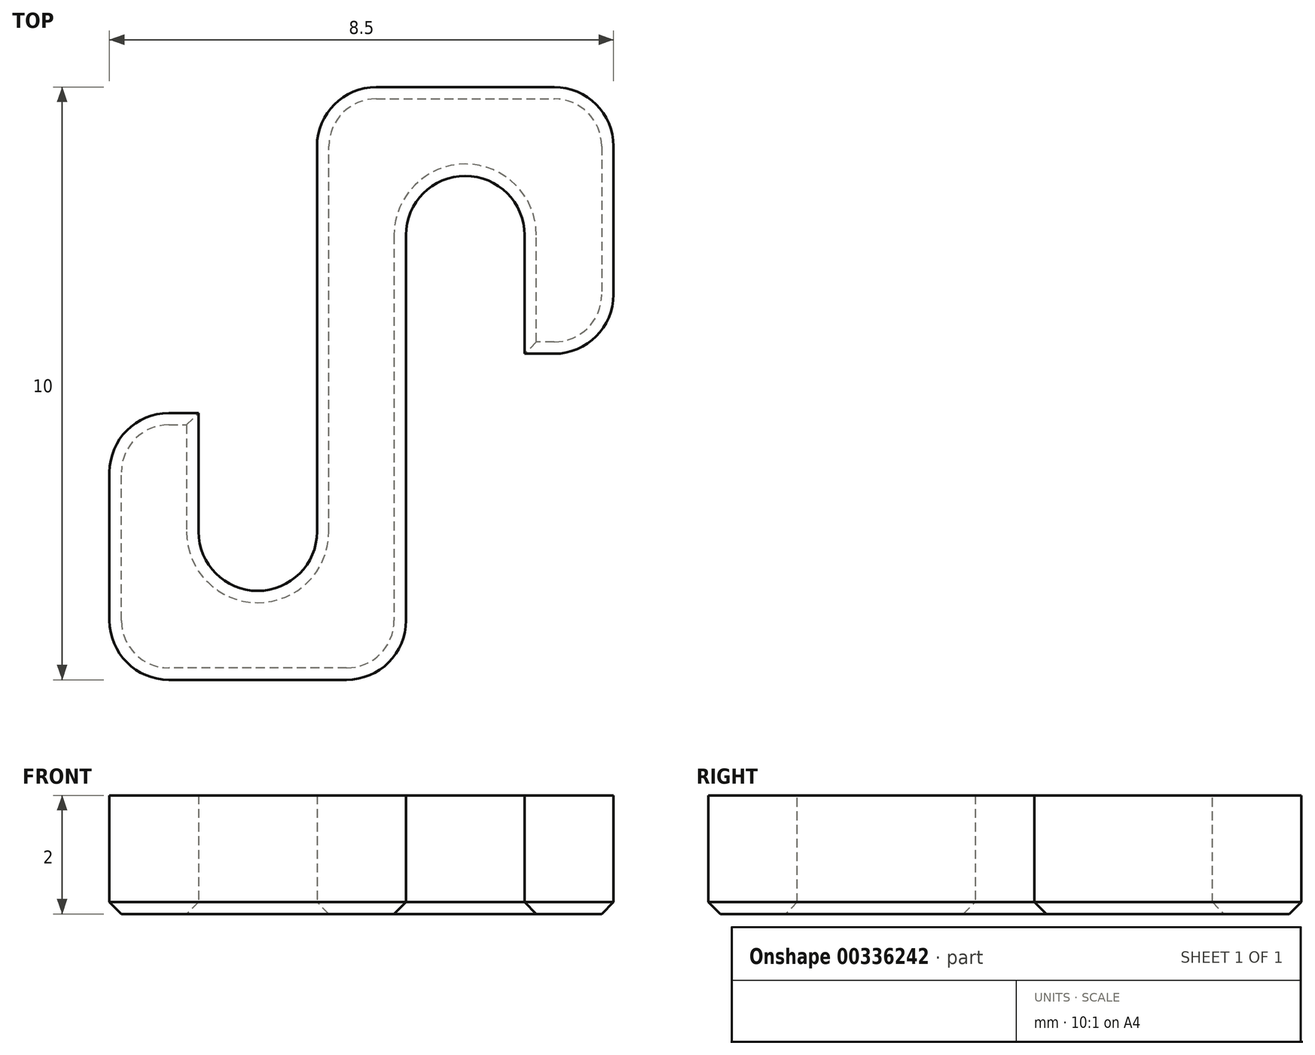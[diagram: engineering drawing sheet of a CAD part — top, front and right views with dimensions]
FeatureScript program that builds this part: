
annotation { "Feature Type Name" : "Feature", "Feature Type Description" : "" }
export const myFeature = defineFeature(function(context is Context, id is Id, definition is map)
    precondition{}
    {
        {
            var Q0;
            Q0=qCreatedBy(makeId("Top.planeOp"),FACE);
            var sketch = newSketch(context, id + "F0", { "sketchPlane" : qUnion([Q0])});
            skLineSegment(sketch, "E0", {"start": v(-0.75, 0) * mm, "end": v(-0.75, 5) * mm});
            skLineSegment(sketch, "E1", {"start": v(-0.75, 5) * mm, "end": v(4.25, 5) * mm});
            skLineSegment(sketch, "E2", {"start": v(4.25, 5) * mm, "end": v(4.25, 0.5) * mm});
            skLineSegment(sketch, "E3", {"start": v(4.25, 0.5) * mm, "end": v(2.75, 0.5) * mm});
            skLineSegment(sketch, "E4", {"start": v(2.75, 0.5) * mm, "end": v(2.75, 3.5) * mm});
            skLineSegment(sketch, "E5", {"start": v(2.75, 3.5) * mm, "end": v(0.75, 3.5) * mm});
            skLineSegment(sketch, "E6", {"start": v(0.75, 3.5) * mm, "end": v(0.75, 0) * mm});
            skLineSegment(sketch, "E7.1.0", {"start": v(0.75, 0) * mm, "end": v(0.75, -5) * mm});
            skLineSegment(sketch, "E7.1.1", {"start": v(-0.75, -3.5) * mm, "end": v(-0.75, 0) * mm});
            skLineSegment(sketch, "E7.1.2", {"start": v(-2.75, -3.5) * mm, "end": v(-0.75, -3.5) * mm});
            skLineSegment(sketch, "E7.1.3", {"start": v(-2.75, -0.5) * mm, "end": v(-2.75, -3.5) * mm});
            skLineSegment(sketch, "E7.1.4", {"start": v(-4.25, -0.5) * mm, "end": v(-2.75, -0.5) * mm});
            skLineSegment(sketch, "E7.1.5", {"start": v(-4.25, -5) * mm, "end": v(-4.25, -0.5) * mm});
            skLineSegment(sketch, "E7.1.6", {"start": v(0.75, -5) * mm, "end": v(-4.25, -5) * mm});
            skPoint(sketch, "E7.center", {"position": v(0, 0) * mm});
            skSolve(sketch);
        }
        {
            var Q0;
            Q0 = qSketchRegion(id + "F0", true);
            extrude(context, id + "F1", {"entities" : qUnion([Q0]), "depth" : 2 * mm, "offsetDistance" : 25 * mm});
        }
        {
            var Q0;
            Q0=makeQuery(id+"F1.opExtrude","SWEPT_EDGE",EDGE,{"disambiguationData":[OSD([sQuery(id+"F0.wireOp",EDGE,"E0"),sQuery(id+"F0.wireOp",EDGE,"E1")])]});
            var Q1;
            Q1=makeQuery(id+"F1.opExtrude","SWEPT_EDGE",EDGE,{"disambiguationData":[OSD([sQuery(id+"F0.wireOp",EDGE,"E5"),sQuery(id+"F0.wireOp",EDGE,"E6")])]});
            var Q2;
            Q2=makeQuery(id+"F1.opExtrude","SWEPT_EDGE",EDGE,{"disambiguationData":[OSD([sQuery(id+"F0.wireOp",EDGE,"E4"),sQuery(id+"F0.wireOp",EDGE,"E5")])]});
            var Q3;
            Q3=makeQuery(id+"F1.opExtrude","SWEPT_EDGE",EDGE,{"disambiguationData":[OSD([sQuery(id+"F0.wireOp",EDGE,"E1"),sQuery(id+"F0.wireOp",EDGE,"E2")])]});
            var Q4;
            Q4=makeQuery(id+"F1.opExtrude","SWEPT_EDGE",EDGE,{"disambiguationData":[OSD([sQuery(id+"F0.wireOp",EDGE,"E2"),sQuery(id+"F0.wireOp",EDGE,"E3")])]});
            var Q5;
            Q5=makeQuery(id+"F1.opExtrude","SWEPT_EDGE",EDGE,{"disambiguationData":[OSD([sQuery(id+"F0.wireOp",EDGE,"E7.1.0"),sQuery(id+"F0.wireOp",EDGE,"E7.1.6")])]});
            var Q6;
            Q6=makeQuery(id+"F1.opExtrude","SWEPT_EDGE",EDGE,{"disambiguationData":[OSD([sQuery(id+"F0.wireOp",EDGE,"E7.1.5"),sQuery(id+"F0.wireOp",EDGE,"E7.1.6")])]});
            var Q7;
            Q7=makeQuery(id+"F1.opExtrude","SWEPT_EDGE",EDGE,{"disambiguationData":[OSD([sQuery(id+"F0.wireOp",EDGE,"E7.1.4"),sQuery(id+"F0.wireOp",EDGE,"E7.1.5")])]});
            var Q8;
            Q8=makeQuery(id+"F1.opExtrude","SWEPT_EDGE",EDGE,{"disambiguationData":[OSD([sQuery(id+"F0.wireOp",EDGE,"E7.1.1"),sQuery(id+"F0.wireOp",EDGE,"E7.1.2")])]});
            var Q9;
            Q9=makeQuery(id+"F1.opExtrude","SWEPT_EDGE",EDGE,{"disambiguationData":[OSD([sQuery(id+"F0.wireOp",EDGE,"E7.1.2"),sQuery(id+"F0.wireOp",EDGE,"E7.1.3")])]});
            fillet(context, id + "F2", {"entities" : qUnion([Q0, Q1, Q2, Q3, Q4, Q5, Q6, Q7, Q8, Q9]), "radius" : 1 * mm, "allowEdgeOverflow" : false});
        }
        {
            var Q0;
            Q0=makeQuery(id+"F1.opExtrude","CAP_FACE",FACE,{"disambiguationData":[OSD([sQuery(id+"F0.wireOp",EDGE,"E0"),sQuery(id+"F0.wireOp",EDGE,"E1"),sQuery(id+"F0.wireOp",EDGE,"E2"),sQuery(id+"F0.wireOp",EDGE,"E3"),sQuery(id+"F0.wireOp",EDGE,"E4"),sQuery(id+"F0.wireOp",EDGE,"E5"),sQuery(id+"F0.wireOp",EDGE,"E6"),sQuery(id+"F0.wireOp",EDGE,"E7.1.0"),sQuery(id+"F0.wireOp",EDGE,"E7.1.1"),sQuery(id+"F0.wireOp",EDGE,"E7.1.2"),sQuery(id+"F0.wireOp",EDGE,"E7.1.3"),sQuery(id+"F0.wireOp",EDGE,"E7.1.4"),sQuery(id+"F0.wireOp",EDGE,"E7.1.5"),sQuery(id+"F0.wireOp",EDGE,"E7.1.6")])],"isStart":true});
            chamfer(context, id + "F3", {"entities" : qUnion([Q0]), "width" : 0.2 * mm});
        }
    });
